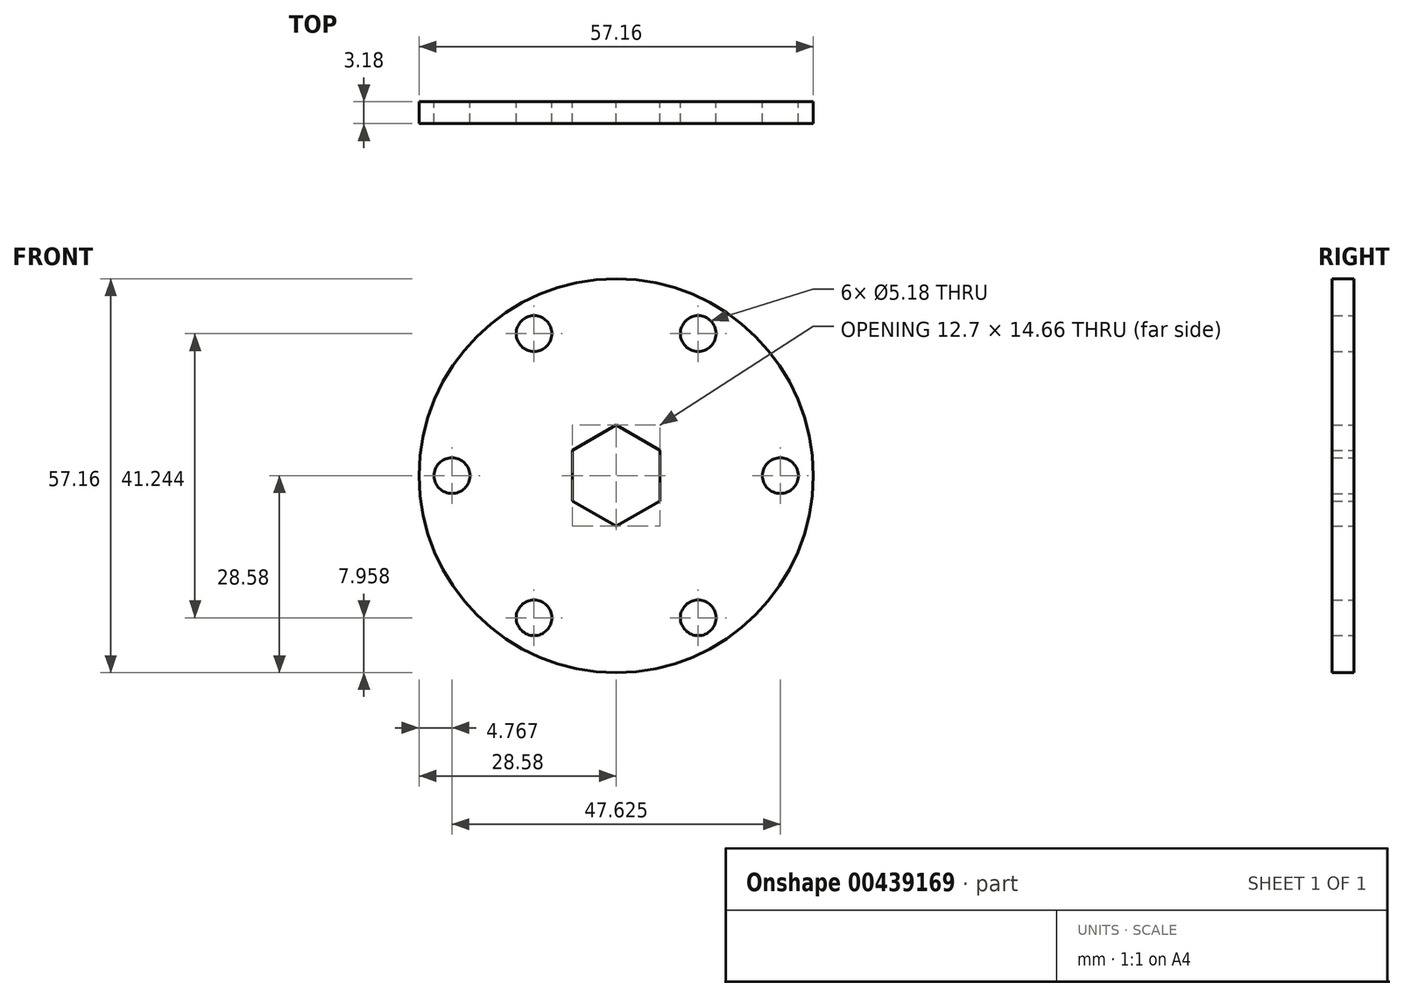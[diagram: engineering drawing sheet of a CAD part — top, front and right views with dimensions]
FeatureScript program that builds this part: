
annotation { "Feature Type Name" : "Feature", "Feature Type Description" : "" }
export const myFeature = defineFeature(function(context is Context, id is Id, definition is map)
    precondition{}
    {
        {
            var Q0;
            Q0=qCreatedBy(makeId("Front.planeOp"),FACE);
            var sketch = newSketch(context, id + "F0", { "sketchPlane" : qUnion([Q0])});
            skCircle(sketch, "E0.0", {"center": v(-11.9, 20.62) * mm, "radius": 2.6 * mm});
            skCircle(sketch, "E0.1", {"center": v(-23.81, 0) * mm, "radius": 2.6 * mm});
            skCircle(sketch, "E0.2", {"center": v(-11.9, -20.62) * mm, "radius": 2.6 * mm});
            skCircle(sketch, "E0.3", {"center": v(11.9, -20.62) * mm, "radius": 2.6 * mm});
            skCircle(sketch, "E0.4", {"center": v(23.81, 0) * mm, "radius": 2.6 * mm});
            skCircle(sketch, "E0.5", {"center": v(11.9, 20.62) * mm, "radius": 2.6 * mm});
            skCircle(sketch, "E1", {"center": v(0, 0) * mm, "radius": 28.58 * mm});
            skCircle(sketch, "E2.cCircle", {"center": v(0, 0) * mm, "radius": 6.35 * mm, "construction": true});
            skLineSegment(sketch, "E2.0", {"start": v(0, 7.33) * mm, "end": v(6.35, 3.67) * mm});
            skLineSegment(sketch, "E2.1", {"start": v(6.35, 3.67) * mm, "end": v(6.35, -3.67) * mm});
            skLineSegment(sketch, "E2.2", {"start": v(6.35, -3.67) * mm, "end": v(0, -7.33) * mm});
            skLineSegment(sketch, "E2.3", {"start": v(0, -7.33) * mm, "end": v(-6.35, -3.67) * mm});
            skLineSegment(sketch, "E2.4", {"start": v(-6.35, -3.67) * mm, "end": v(-6.35, 3.67) * mm});
            skLineSegment(sketch, "E2.5", {"start": v(-6.35, 3.67) * mm, "end": v(0, 7.33) * mm});
            skPoint(sketch, "E2.0.midPoint", {"position": v(3.18, 5.5) * mm});
            skCircle(sketch, "E3.cCircle", {"center": v(0, 0) * mm, "radius": 23.81 * mm, "construction": true});
            skLineSegment(sketch, "E3.0", {"start": v(11.9, 20.62) * mm, "end": v(23.81, 0) * mm, "construction": true});
            skLineSegment(sketch, "E3.1", {"start": v(23.81, 0) * mm, "end": v(11.9, -20.62) * mm, "construction": true});
            skLineSegment(sketch, "E3.2", {"start": v(11.9, -20.62) * mm, "end": v(-11.9, -20.62) * mm, "construction": true});
            skLineSegment(sketch, "E3.3", {"start": v(-11.9, -20.62) * mm, "end": v(-23.81, 0) * mm, "construction": true});
            skLineSegment(sketch, "E3.4", {"start": v(-23.81, 0) * mm, "end": v(-11.9, 20.62) * mm, "construction": true});
            skLineSegment(sketch, "E3.5", {"start": v(-11.9, 20.62) * mm, "end": v(11.9, 20.62) * mm, "construction": true});
            skSolve(sketch);
        }
        {
            var Q0;
            Q0=makeQuery(id+"F0.imprint","IMPRINT",FACE,{"disambiguationData":[TD([[makeQuery(id+"F0.imprint","IMPRINT",EDGE,{"derivedFrom":sQuery(id+"F0.wireOp",EDGE,"E0.0")}),-1.0]])]});
            extrude(context, id + "F1", {"entities" : qUnion([Q0]), "depth" : 3.17 * mm});
        }
    });
